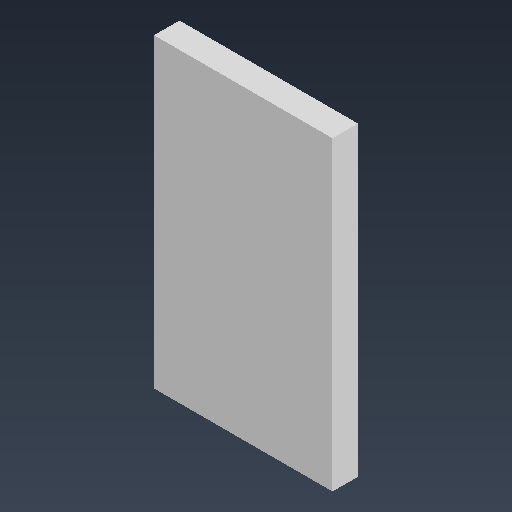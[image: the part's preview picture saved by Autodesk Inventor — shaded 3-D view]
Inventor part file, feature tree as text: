
AUTODESK INVENTOR PART (.ipt)
format: ipt  version: 2025.3 (Build 293356000, 356)  size: 79,872 bytes
history: native  units: mm
features: extrude x1, sketch x1
ambient origin geometry x8: Origin, YZ Plane, XZ Plane, XY Plane, X Axis, Y Axis, Z Axis, Center Point
bodies: Solid1 (feature_tree)
feature tree (2):
  extrude  "Extrusion1"  Depth=5.0mm
  sketch  "Sketch1"  dims[d0=35.0mm d1=5.0mm d2=60.0mm d3=0.0mm]
